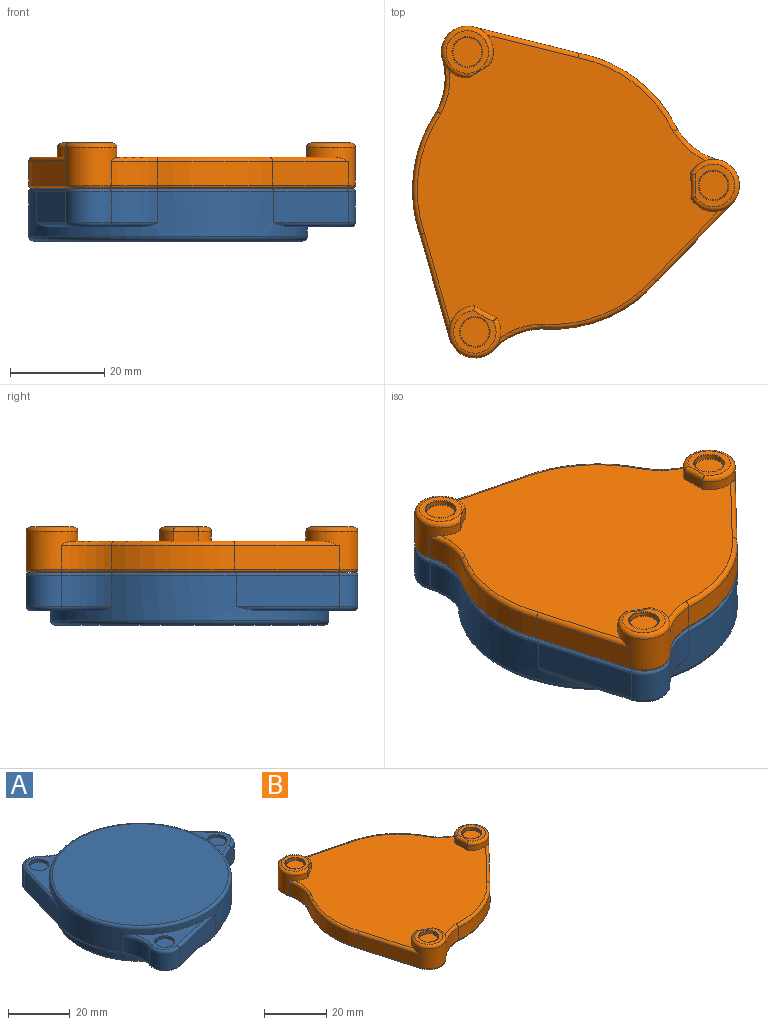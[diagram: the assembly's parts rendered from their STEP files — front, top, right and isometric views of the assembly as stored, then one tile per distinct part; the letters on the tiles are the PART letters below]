
ASSEMBLY  parts=2 mates=1
PART A: 68 faces, bbox 72.1x71.2x15.1 mm
  f0: cylinder r=5.5mm len=7.52mm, axis (0,0,1), area 77.2mm2, adj f7,f8,f14,f55
  f1: plane 68.85x67.81mm, normal (0,0,-1), area 573.3mm2, adj f10,f26,f41,f49,f54,f55,f56,f57
  f2: plane 21.71x14.18mm, normal (0,0,1), area 83.4mm2, adj f11,f13,f14,f15,f16
  f3: cylinder r=3.15mm len=6.3mm, axis (0,0,1), area 17.8mm2, adj f11,f12
  f4: plane 6.1x6.1mm, normal (0,0,1), area 29.2mm2, adj f12
  f5: cylinder r=3.15mm len=6.3mm, axis (0,0,1), area 17.8mm2, adj f9,f10
  f6: plane 6.1x6.1mm, normal (0,0,-1), area 29.2mm2, adj f9
  f7: cylinder r=14.6mm len=10.56mm, axis (0,0,1), area 69.8mm2, adj f0,f13,f16,f56
  f8: plane 21.91x6.4mm, normal (0.24,-0.97,0), area 144.5mm2, adj f0,f15,f16,f54
  f9: torus R=3.05mm, axis (0,0,1), area 3.1mm2, adj f5,f6
  f10: torus R=3.25mm, axis (0,0,1), area 3.1mm2, adj f1,f5
  f11: torus R=3.25mm, axis (0,0,1), area 3.1mm2, adj f2,f3
  f12: torus R=3.05mm, axis (0,0,1), area 3.1mm2, adj f3,f4
  f13: torus R=15.6mm, axis (0,0,1), area 15mm2, adj f2,f7,f14,f16
  f14: torus R=4.5mm, axis (0,0,1), area 17.8mm2, adj f0,f2,f13,f15
  f15: cylinder r=1mm len=22.15mm, axis (0.97,0.24,0), area 31.2mm2, adj f2,f8,f14,f16
  f16: cylinder r=29.5mm len=59mm, axis (0,0,1), area 994.1mm2, adj f2,f7,f8,f13,f15,f18,f23,f24
  f17: cylinder r=5.5mm len=9.6mm, axis (0,0,1), area 77.2mm2, adj f23,f24,f30,f59
  f18: plane 19.39x19.25mm, normal (0,0,1), area 83.4mm2, adj f16,f27,f29,f30,f31
  f19: cylinder r=3.15mm len=6.3mm, axis (0,0,1), area 17.8mm2, adj f27,f28
  f20: plane 6.1x6.1mm, normal (0,0,1), area 29.2mm2, adj f28
  f21: cylinder r=3.15mm len=6.3mm, axis (0,0,1), area 17.8mm2, adj f25,f26
  f22: plane 6.1x6.1mm, normal (0,0,-1), area 29.2mm2, adj f25
  f23: cylinder r=14.6mm len=9.84mm, axis (0,0,1), area 69.8mm2, adj f16,f17,f29,f61
  f24: plane 21.72x6.4mm, normal (-0.96,0.27,0), area 144.5mm2, adj f16,f17,f31,f58
  f25: torus R=3.05mm, axis (0,0,1), area 3.1mm2, adj f21,f22
  f26: torus R=3.25mm, axis (0,0,1), area 3.1mm2, adj f1,f21
  f27: torus R=3.25mm, axis (0,0,1), area 3.1mm2, adj f18,f19
  f28: torus R=3.05mm, axis (0,0,1), area 3.1mm2, adj f19,f20
  f29: torus R=15.6mm, axis (0,0,1), area 15mm2, adj f16,f18,f23,f30
  f30: torus R=4.5mm, axis (0,0,1), area 17.8mm2, adj f17,f18,f29,f31
  f31: cylinder r=1mm len=21.99mm, axis (-0.27,-0.96,0), area 31.2mm2, adj f16,f18,f24,f30
  f32: cylinder r=5.5mm len=9.27mm, axis (0,0,1), area 77.2mm2, adj f38,f39,f45,f62
  f33: plane 23.58x12.83mm, normal (0,0,1), area 83.4mm2, adj f16,f42,f44,f45,f46
  f34: cylinder r=3.15mm len=6.3mm, axis (0,0,1), area 17.8mm2, adj f42,f43
  f35: plane 6.1x6.1mm, normal (0,0,1), area 29.2mm2, adj f43
  f36: cylinder r=3.15mm len=6.3mm, axis (0,0,1), area 17.8mm2, adj f40,f41
  f37: plane 6.1x6.1mm, normal (0,0,-1), area 29.2mm2, adj f40
  f38: cylinder r=14.6mm len=8.45mm, axis (0,0,1), area 69.8mm2, adj f16,f32,f44,f60
  f39: plane 16.23x15.71mm, normal (0.72,0.7,0), area 144.5mm2, adj f16,f32,f46,f64
  f40: torus R=3.05mm, axis (0,0,1), area 3.1mm2, adj f36,f37
  f41: torus R=3.25mm, axis (0,0,1), area 3.1mm2, adj f1,f36
  f42: torus R=3.25mm, axis (0,0,1), area 3.1mm2, adj f33,f34
  f43: torus R=3.05mm, axis (0,0,1), area 3.1mm2, adj f34,f35
  f44: torus R=15.6mm, axis (0,0,1), area 15mm2, adj f16,f33,f38,f45
  f45: torus R=4.5mm, axis (0,0,1), area 17.8mm2, adj f32,f33,f44,f46
  f46: cylinder r=1mm len=16.92mm, axis (-0.7,0.72,0), area 31.2mm2, adj f16,f33,f39,f45
  f47: cylinder r=25.5mm len=51mm, axis (0,0,1), area 1393.9mm2, adj f53,f65
  f48: plane 54.4x54.4mm, normal (0,0,-1), area 233.1mm2, adj f65,f66
  f49: cylinder r=27.5mm len=55mm, axis (0,0,1), area 639.3mm2, adj f1,f66
  f50: plane 57x57mm, normal (0,0,1), area 2551.8mm2, adj f52
  f51: plane 44x44mm, normal (0,0,-1), area 1520.5mm2, adj f53
  f52: torus R=28.5mm, axis (0,0,1), area 287.6mm2, adj f16,f50
  f53: torus R=22mm, axis (0,0,1), area 836.9mm2, adj f47,f51
  f54: cylinder r=0.7mm len=22.1mm, axis (-0.97,-0.24,0), area 24.8mm2, adj f1,f8,f55,f67
  f55: torus R=4.8mm, axis (0,0,1), area 12.7mm2, adj f0,f1,f54,f56
  f56: torus R=15.3mm, axis (0,0,1), area 12.2mm2, adj f1,f7,f55,f57
  f57: torus R=28.8mm, axis (0,0,1), area 30.2mm2, adj f1,f16,f56,f58
  f58: cylinder r=0.7mm len=21.93mm, axis (0.27,0.96,0), area 24.8mm2, adj f1,f24,f57,f59
  f59: torus R=4.8mm, axis (0,0,1), area 12.7mm2, adj f1,f17,f58,f61
  f60: torus R=15.3mm, axis (0,0,1), area 12.2mm2, adj f1,f38,f62,f67
  f61: torus R=15.3mm, axis (0,0,1), area 12.2mm2, adj f1,f23,f59,f63
  f62: torus R=4.8mm, axis (0,0,1), area 12.7mm2, adj f1,f32,f60,f64
  f63: torus R=28.8mm, axis (0,0,1), area 30.2mm2, adj f1,f16,f61,f64
  f64: cylinder r=0.7mm len=16.73mm, axis (0.7,-0.72,0), area 24.8mm2, adj f1,f39,f62,f63
  f65: torus R=25.8mm, axis (0,0,-1), area 75.8mm2, adj f47,f48
  f66: torus R=27.2mm, axis (0,0,-1), area 81.1mm2, adj f48,f49
  f67: torus R=28.8mm, axis (0,0,1), area 30.2mm2, adj f1,f16,f54,f60
PART B: 74 faces, bbox 72.1x71.2x9.6 mm
  f0: cylinder r=29.5mm len=24.38mm, axis (0,0,1), area 133.9mm2, adj f39,f48,f60,f72
  f1: cylinder r=29.5mm len=26.12mm, axis (0,0,1), area 133.9mm2, adj f11,f49,f58,f73
  f2: cylinder r=29.5mm len=20.86mm, axis (0,0,1), area 133.9mm2, adj f13,f37,f62,f71
  f3: cylinder r=29.5mm len=4.46mm, axis (0,0,-1), area 14.8mm2, adj f4,f12,f68
  f4: cylinder r=5.5mm len=11mm, axis (0,0,-1), area 132.2mm2, adj f3,f11,f12,f13,f20,f22,f63,f68
  f5: plane 9x9mm, normal (0,0,1), area 30.4mm2, adj f17,f68
  f6: plane 68.85x67.81mm, normal (0,0,-1), area 521.9mm2, adj f18,f21,f22,f23,f32,f33,f36,f40
  f7: cylinder r=3.15mm len=6.3mm, axis (0,0,-1), area 17.8mm2, adj f18,f19
  f8: plane 6.1x6.1mm, normal (0,0,-1), area 29.2mm2, adj f19
  f9: cylinder r=3.15mm len=6.3mm, axis (0,0,-1), area 17.8mm2, adj f16,f17
  f10: plane 6.1x6.1mm, normal (0,0,1), area 29.2mm2, adj f16
  f11: cylinder r=14.6mm len=10.56mm, axis (0,0,-1), area 53.4mm2, adj f1,f4,f20,f21
  f12: plane 64.1x63.75mm, normal (0,0,1), area 2752mm2, adj f3,f4,f20,f34,f35,f38,f41,f42
  f13: plane 22.26x5.56mm, normal (0.24,0.97,0), area 112.4mm2, adj f2,f4,f23,f63
  f14: plane 54.4x54.4mm, normal (0,0,-1), area 2324.3mm2, adj f69
  f15: cylinder r=27.5mm len=55mm, axis (0,0,1), area 587.5mm2, adj f69,f70
  f16: torus R=3.05mm, axis (0,0,-1), area 3.1mm2, adj f9,f10
  f17: torus R=3.25mm, axis (0,0,-1), area 3.1mm2, adj f5,f9
  f18: torus R=3.25mm, axis (0,0,-1), area 3.1mm2, adj f6,f7
  f19: torus R=3.05mm, axis (0,0,-1), area 3.1mm2, adj f7,f8
  f20: torus R=15.6mm, axis (0,0,-1), area 15.9mm2, adj f4,f11,f12,f58
  f21: torus R=15.3mm, axis (0,0,-1), area 12.2mm2, adj f6,f11,f22,f73
  f22: torus R=4.8mm, axis (0,0,-1), area 12.7mm2, adj f4,f6,f21,f23
  f23: cylinder r=0.7mm len=22.45mm, axis (0.97,-0.24,0), area 25.2mm2, adj f6,f13,f22,f71
  f24: plane 6.1x6.1mm, normal (0,0,1), area 29.2mm2, adj f25
  f25: torus R=3.05mm, axis (0,0,-1), area 3.1mm2, adj f24,f27
  f26: plane 6.1x6.1mm, normal (0,0,-1), area 29.2mm2, adj f28
  f27: cylinder r=3.15mm len=6.3mm, axis (0,0,-1), area 17.8mm2, adj f25,f29
  f28: torus R=3.05mm, axis (0,0,-1), area 3.1mm2, adj f26,f30
  f29: torus R=3.25mm, axis (0,0,-1), area 3.1mm2, adj f27,f31
  f30: cylinder r=3.15mm len=6.3mm, axis (0,0,-1), area 17.8mm2, adj f28,f32
  f31: plane 9x8.38mm, normal (0,0,1), area 27.9mm2, adj f29,f66,f67
  f32: torus R=3.25mm, axis (0,0,-1), area 3.1mm2, adj f6,f30
  f33: torus R=4.8mm, axis (0,0,-1), area 12.7mm2, adj f6,f35,f36,f40
  f34: cylinder r=29.5mm len=5.23mm, axis (0,0,-1), area 10.5mm2, adj f12,f35,f67
  f35: cylinder r=5.5mm len=11mm, axis (0,0,-1), area 132.2mm2, adj f12,f33,f34,f37,f38,f39,f61,f66
  f36: torus R=15.3mm, axis (0,0,-1), area 12.2mm2, adj f6,f33,f37,f71
  f37: cylinder r=14.6mm len=8.45mm, axis (0,0,-1), area 53.4mm2, adj f2,f35,f36,f38
  f38: torus R=15.6mm, axis (0,0,-1), area 15.9mm2, adj f12,f35,f37,f62
  f39: plane 16.5x15.94mm, normal (0.72,-0.69,0), area 112.4mm2, adj f0,f35,f40,f61
  f40: cylinder r=0.7mm len=17mm, axis (-0.69,-0.72,0), area 25.2mm2, adj f6,f33,f39,f72
  f41: cylinder r=29.5mm len=4.6mm, axis (0,0,-1), area 10.5mm2, adj f12,f42,f65
  f42: cylinder r=5.5mm len=11mm, axis (0,0,-1), area 132.2mm2, adj f12,f41,f48,f49,f54,f56,f59,f64
  f43: plane 9x8.99mm, normal (0,0,1), area 27.9mm2, adj f50,f64,f65
  f44: cylinder r=3.15mm len=6.3mm, axis (0,0,-1), area 17.8mm2, adj f52,f53
  f45: plane 6.1x6.1mm, normal (0,0,-1), area 29.2mm2, adj f52
  f46: cylinder r=3.15mm len=6.3mm, axis (0,0,-1), area 17.8mm2, adj f50,f51
  f47: plane 6.1x6.1mm, normal (0,0,1), area 29.2mm2, adj f51
  f48: cylinder r=14.6mm len=9.84mm, axis (0,0,-1), area 53.4mm2, adj f0,f42,f54,f55
  f49: plane 22.06x6.32mm, normal (-0.96,-0.28,0), area 112.4mm2, adj f1,f42,f57,f59
  f50: torus R=3.25mm, axis (0,0,-1), area 3.1mm2, adj f43,f46
  f51: torus R=3.05mm, axis (0,0,-1), area 3.1mm2, adj f46,f47
  f52: torus R=3.05mm, axis (0,0,-1), area 3.1mm2, adj f44,f45
  f53: torus R=3.25mm, axis (0,0,-1), area 3.1mm2, adj f6,f44
  f54: torus R=15.6mm, axis (0,0,-1), area 15.9mm2, adj f12,f42,f48,f60
  f55: torus R=15.3mm, axis (0,0,-1), area 12.2mm2, adj f6,f48,f56,f72
  f56: torus R=4.8mm, axis (0,0,-1), area 12.7mm2, adj f6,f42,f55,f57
  f57: cylinder r=0.7mm len=22.27mm, axis (-0.28,0.96,0), area 25.2mm2, adj f6,f49,f56,f73
  f58: torus R=28.5mm, axis (0,0,-1), area 42.4mm2, adj f1,f12,f20,f59
  f59: cylinder r=1mm len=22.36mm, axis (0.28,-0.96,0), area 33.6mm2, adj f12,f42,f49,f58
  f60: torus R=28.5mm, axis (0,0,-1), area 42.4mm2, adj f0,f12,f54,f61
  f61: cylinder r=1mm len=17.21mm, axis (0.69,0.72,0), area 33.6mm2, adj f12,f35,f39,f60
  f62: torus R=28.5mm, axis (0,0,-1), area 42.4mm2, adj f2,f12,f38,f63
  f63: cylinder r=1mm len=22.53mm, axis (-0.97,0.24,0), area 33.6mm2, adj f4,f12,f13,f62
  f64: torus R=4.5mm, axis (0,0,-1), area 42.2mm2, adj f42,f43,f65
  f65: torus R=30.5mm, axis (0,0,-1), area 7.8mm2, adj f41,f43,f64
  f66: torus R=4.5mm, axis (0,0,-1), area 42.2mm2, adj f31,f35,f67
  f67: torus R=30.5mm, axis (0,0,-1), area 7.8mm2, adj f31,f34,f66
  f68: torus R=4.5mm, axis (0,0,-1), area 45.2mm2, adj f3,f4,f5
  f69: torus R=27.2mm, axis (0,0,1), area 81.1mm2, adj f14,f15
  f70: torus R=27.8mm, axis (0,0,-1), area 81.7mm2, adj f6,f15
  f71: torus R=28.8mm, axis (0,0,-1), area 29.8mm2, adj f2,f6,f23,f36
  f72: torus R=28.8mm, axis (0,0,-1), area 29.8mm2, adj f0,f6,f40,f55
  f73: torus R=28.8mm, axis (0,0,-1), area 29.8mm2, adj f1,f6,f21,f57
PLACE A rot(axis=(1,0,0),180deg) t=(0,0,5.75)mm
PLACE B t=(0,0,13.9)mm
MATE revolute A.f53 <-> B.f0  axis (0,0,-1) through (0,0,16.1)mm
